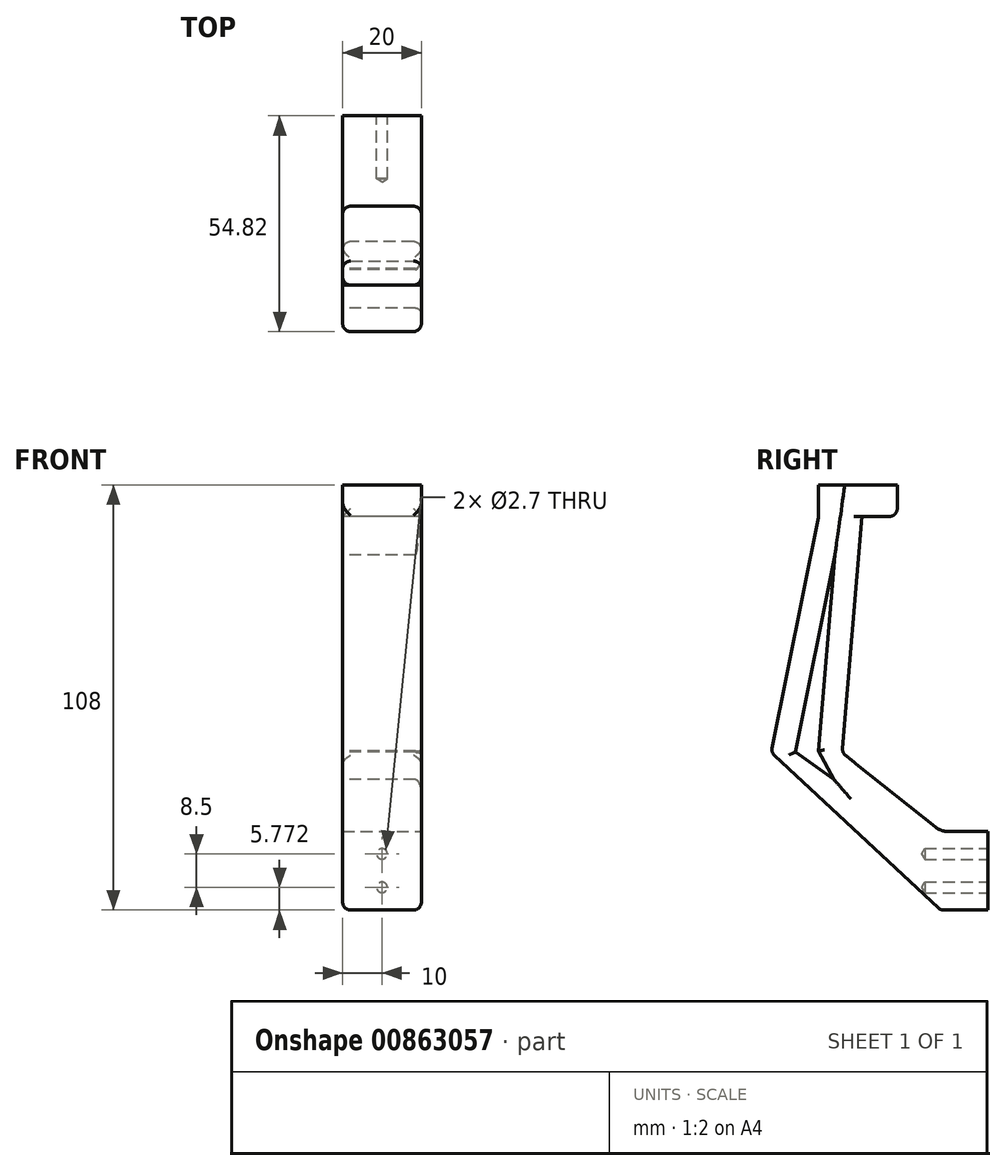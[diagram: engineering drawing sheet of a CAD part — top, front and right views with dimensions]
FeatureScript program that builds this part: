
annotation { "Feature Type Name" : "Feature", "Feature Type Description" : "" }
export const myFeature = defineFeature(function(context is Context, id is Id, definition is map)
    precondition{}
    {
        {
            var Q0;
            Q0=qCreatedBy(makeId("Front.planeOp"),FACE);
            var sketch = newSketch(context, id + "F0", { "sketchPlane" : qUnion([Q0])});
            skLineSegment(sketch, "E0.bottom", {"start": v(-10, -10) * mm, "end": v(10, -10) * mm});
            skLineSegment(sketch, "E0.top", {"start": v(-10, 10) * mm, "end": v(10, 10) * mm});
            skLineSegment(sketch, "E0.left", {"start": v(-10, -10) * mm, "end": v(-10, 10) * mm});
            skLineSegment(sketch, "E0.right", {"start": v(10, -10) * mm, "end": v(10, 10) * mm});
            skPoint(sketch, "E0.middle", {"position": v(0, 0) * mm});
            skSolve(sketch);
        }
        {
            var Q0;
            Q0=qCreatedBy(makeId("Top.planeOp"),FACE);
            cPlane(context, id + "F1", {"entities" : qUnion([Q0]), "cplaneType" : CPlaneType.OFFSET, "offset" : 30 * mm, "width" : 150 * mm, "height" : 150 * mm});
        }
        {
            var Q0;
            Q0=qCreatedBy(id+"F1.planeOp",FACE);
            var sketch = newSketch(context, id + "F2", { "sketchPlane" : qUnion([Q0])});
            skLineSegment(sketch, "E1.bottom", {"start": v(10, -43) * mm, "end": v(-10, -43) * mm});
            skLineSegment(sketch, "E1.top", {"start": v(10, -25) * mm, "end": v(-10, -25) * mm});
            skLineSegment(sketch, "E1.left", {"start": v(10, -43) * mm, "end": v(10, -25) * mm});
            skLineSegment(sketch, "E1.right", {"start": v(-10, -43) * mm, "end": v(-10, -25) * mm});
            skPoint(sketch, "E1.middle", {"position": v(0, -34) * mm});
            skSolve(sketch);
        }
        {
            var Q0;
            Q0=makeQuery(id+"F0.imprint","IMPRINT",FACE,{"disambiguationData":[TD([[makeQuery(id+"F0.imprint","IMPRINT",EDGE,{"derivedFrom":sQuery(id+"F0.wireOp",EDGE,"E0.bottom")}),1.0]])]});
            var Q1;
            Q1=makeQuery(id+"F2.imprint","IMPRINT",FACE,{"disambiguationData":[TD([[makeQuery(id+"F2.imprint","IMPRINT",EDGE,{"derivedFrom":sQuery(id+"F2.wireOp",EDGE,"E1.bottom")}),-1.0]])]});
            loft(context, id + "F3", {"sheetProfilesArray" : [{ "sheetProfileEntities" : qUnion([Q0]) }, { "sheetProfileEntities" : qUnion([Q1]) }]});
        }
        {
            var Q0;
            Q0=qCreatedBy(makeId("Top.planeOp"),FACE);
            cPlane(context, id + "F4", {"entities" : qUnion([Q0]), "cplaneType" : CPlaneType.OFFSET, "offset" : 90 * mm, "width" : 150 * mm, "height" : 150 * mm});
        }
        {
            var Q0;
            Q0=qCreatedBy(id+"F4.planeOp",FACE);
            var sketch = newSketch(context, id + "F5", { "sketchPlane" : qUnion([Q0])});
            skLineSegment(sketch, "E2.bottom", {"start": v(10, -31) * mm, "end": v(-10, -31) * mm});
            skLineSegment(sketch, "E2.top", {"start": v(10, -20) * mm, "end": v(-10, -20) * mm});
            skLineSegment(sketch, "E2.left", {"start": v(10, -31) * mm, "end": v(10, -20) * mm});
            skLineSegment(sketch, "E2.right", {"start": v(-10, -31) * mm, "end": v(-10, -20) * mm});
            skPoint(sketch, "E2.middle", {"position": v(0, -25.5) * mm});
            skSolve(sketch);
        }
        {
            var Q1;
            Q1=makeQuery(id+"F5.imprint","IMPRINT",FACE,{"disambiguationData":[TD([[makeQuery(id+"F5.imprint","IMPRINT",EDGE,{"derivedFrom":sQuery(id+"F5.wireOp",EDGE,"E2.bottom")}),-1.0]])]});
            var Q2;
            Q2=makeQuery(id+"F3.opLoft","CAP_FACE",FACE,{"disambiguationData":[OSD([makeQuery(id+"F2.imprint","IMPRINT",FACE,{"disambiguationData":[TD([[makeQuery(id+"F2.imprint","IMPRINT",EDGE,{"derivedFrom":sQuery(id+"F2.wireOp",EDGE,"E1.bottom")}),-1.0]])]})])],"isStart":true});
            loft(context, id + "F6", {"operationType" : NewBodyOperationType.ADD, "sheetProfilesArray" : [{ "sheetProfileEntities" : qUnion([Q1]) }, { "sheetProfileEntities" : qUnion([Q2]) }]});
        }
        {
            var Q0;
            Q0=qCreatedBy(id+"F4.planeOp",FACE);
            var sketch = newSketch(context, id + "F7", { "sketchPlane" : qUnion([Q0])});
            skLineSegment(sketch, "E3.bottom", {"start": v(10, -31) * mm, "end": v(-10, -31) * mm});
            skLineSegment(sketch, "E3.top", {"start": v(10, -11) * mm, "end": v(-10, -11) * mm});
            skLineSegment(sketch, "E3.left", {"start": v(10, -31) * mm, "end": v(10, -11) * mm});
            skLineSegment(sketch, "E3.right", {"start": v(-10, -31) * mm, "end": v(-10, -11) * mm});
            skPoint(sketch, "E3.middle", {"position": v(0, -21) * mm});
            skSolve(sketch);
        }
        {
            var Q0;
            Q0=makeQuery(id+"F7.imprint","IMPRINT",FACE,{"disambiguationData":[TD([[makeQuery(id+"F7.imprint","IMPRINT",EDGE,{"derivedFrom":sQuery(id+"F7.wireOp",EDGE,"E3.bottom")}),-1.0]])]});
            extrude(context, id + "F8", {"entities" : qUnion([Q0]), "operationType" : NewBodyOperationType.ADD, "depth" : 8 * mm, "offsetDistance" : 25 * mm});
        }
        {
            var Q0;
            Q0=makeQuery(id+"F3.opLoft","CAP_FACE",FACE,{"disambiguationData":[OSD([makeQuery(id+"F0.imprint","IMPRINT",FACE,{"disambiguationData":[TD([[makeQuery(id+"F0.imprint","IMPRINT",EDGE,{"derivedFrom":sQuery(id+"F0.wireOp",EDGE,"E0.bottom")}),1.0]])]})])],"isStart":true});
            extrude(context, id + "F9", {"entities" : qUnion([Q0]), "operationType" : NewBodyOperationType.ADD, "depth" : 12 * mm, "offsetDistance" : 25 * mm});
        }
        {
            var Q0;
            {var subQ0=sQuery(id+"F0.wireOp",EDGE,"E0.right");var subQ1=sQuery(id+"F0.wireOp",EDGE,"E0.left");var subQ2=sQuery(id+"F0.wireOp",EDGE,"E0.top");Q0=makeQuery(id+"F9.boolean.opBoolean","MERGE",EDGE,{"derivedFrom":[makeQuery(id+"F3.opLoft","MID_CAP_EDGE",EDGE,{"disambiguationData":[OSD([subQ2,subQ1,subQ0])],"capPos":0.0}),makeQuery(id+"F9.opExtrude","CAP_EDGE",EDGE,{"disambiguationData":[OSD([subQ2,subQ1,subQ0])],"isStart":true})]});}
            fillet(context, id + "F10", {"entities" : qUnion([Q0]), "radius" : 5 * mm, "tangentPropagation" : true, "allowEdgeOverflow" : false});
        }
        {
            var Q0;
            {var subQ0=sQuery(id+"F0.wireOp",EDGE,"E0.left");var subQ1=sQuery(id+"F0.wireOp",EDGE,"E0.top");var subQ2=sQuery(id+"F0.wireOp",EDGE,"E0.bottom");var subQ3=sQuery(id+"F2.wireOp",EDGE,"E1.right");var subQ4=sQuery(id+"F2.wireOp",EDGE,"E1.top");var subQ5=sQuery(id+"F2.wireOp",EDGE,"E1.bottom");Q0=makeQuery(id+"F9.boolean.opBoolean","MERGE",FACE,{"derivedFrom":[makeQuery(id+"F8.boolean.opBoolean","MERGE",FACE,{"derivedFrom":[makeQuery(id+"F6.boolean.opBoolean","MERGE",FACE,{"derivedFrom":[makeQuery(id+"F3.opLoft","SWEPT_FACE",FACE,{"disambiguationData":[OSD([subQ2,subQ1,subQ0,subQ5,subQ4,subQ3])]}),makeQuery(id+"F6.opLoft","SWEPT_FACE",FACE,{"disambiguationData":[OSD([subQ5,subQ4,subQ3,sQuery(id+"F5.wireOp",EDGE,"E2.bottom"),sQuery(id+"F5.wireOp",EDGE,"E2.top"),sQuery(id+"F5.wireOp",EDGE,"E2.right")])]})]}),makeQuery(id+"F8.opExtrude","SWEPT_FACE",FACE,{"disambiguationData":[OSD([sQuery(id+"F7.wireOp",EDGE,"E3.right")])]})]}),makeQuery(id+"F9.opExtrude","SWEPT_FACE",FACE,{"disambiguationData":[OSD([subQ2,subQ1,subQ0])]})]});}
            var sketch = newSketch(context, id + "F11", { "sketchPlane" : qUnion([Q0])});
            skLineSegment(sketch, "E4.0", {"start": v(26.83, 80.23) * mm, "end": v(30.99, 30.4) * mm});
            skLineSegment(sketch, "E5.0", {"start": v(26.83, 80.23) * mm, "end": v(36.86, 30.12) * mm});
            skLineSegment(sketch, "E6", {"start": v(30.99, 30.4) * mm, "end": v(27.14, 23.2) * mm});
            skLineSegment(sketch, "E7", {"start": v(27.14, 23.2) * mm, "end": v(36.86, 30.12) * mm});
            skSolve(sketch);
        }
        {
            var Q0;
            Q0=makeQuery(id+"F11.imprint","IMPRINT",FACE,{"disambiguationData":[TD([[makeQuery(id+"F11.imprint","IMPRINT",EDGE,{"derivedFrom":sQuery(id+"F11.wireOp",EDGE,"E4.0")}),1.0]])]});
            extrude(context, id + "F12", {"entities" : qUnion([Q0]), "operationType" : NewBodyOperationType.REMOVE, "oppositeDirection" : true, "depth" : 25 * mm, "offsetDistance" : 25 * mm});
        }
        {
            var Q0;
            Q0=makeQuery(id+"F6.opLoft","MID_CAP_EDGE",EDGE,{"disambiguationData":[OSD([sQuery(id+"F5.wireOp",EDGE,"E2.top"),sQuery(id+"F5.wireOp",EDGE,"E2.left"),sQuery(id+"F5.wireOp",EDGE,"E2.right")])],"capPos":0.0});
            var Q1;
            {var subQ0=sQuery(id+"F2.wireOp",EDGE,"E1.right");var subQ1=sQuery(id+"F2.wireOp",EDGE,"E1.left");var subQ2=sQuery(id+"F2.wireOp",EDGE,"E1.top");Q1=makeQuery(id+"F6.boolean.opBoolean","MERGE",EDGE,{"derivedFrom":[makeQuery(id+"F3.opLoft","MID_CAP_EDGE",EDGE,{"disambiguationData":[OSD([subQ2,subQ1,subQ0])],"capPos":1.0}),makeQuery(id+"F6.opLoft","MID_CAP_EDGE",EDGE,{"disambiguationData":[OSD([subQ2,subQ1,subQ0])],"capPos":1.0})]});}
            var Q2;
            {var subQ0=sQuery(id+"F2.wireOp",EDGE,"E1.right");var subQ1=sQuery(id+"F2.wireOp",EDGE,"E1.left");var subQ2=sQuery(id+"F2.wireOp",EDGE,"E1.bottom");Q2=makeQuery(id+"F6.boolean.opBoolean","MERGE",EDGE,{"derivedFrom":[makeQuery(id+"F3.opLoft","MID_CAP_EDGE",EDGE,{"disambiguationData":[OSD([subQ2,subQ1,subQ0])],"capPos":1.0}),makeQuery(id+"F6.opLoft","MID_CAP_EDGE",EDGE,{"disambiguationData":[OSD([subQ2,subQ1,subQ0])],"capPos":1.0})]});}
            var Q3;
            Q3=makeQuery(id+"F6.opLoft","SWEPT_EDGE",EDGE,{"disambiguationData":[OSD([sQuery(id+"F2.wireOp",EDGE,"E1.bottom"),sQuery(id+"F2.wireOp",EDGE,"E1.left"),sQuery(id+"F5.wireOp",EDGE,"E2.bottom"),sQuery(id+"F5.wireOp",EDGE,"E2.left")])]});
            var Q4;
            Q4=makeQuery(id+"F3.opLoft","SWEPT_EDGE",EDGE,{"disambiguationData":[OSD([sQuery(id+"F0.wireOp",EDGE,"E0.bottom"),sQuery(id+"F0.wireOp",EDGE,"E0.right"),sQuery(id+"F2.wireOp",EDGE,"E1.bottom"),sQuery(id+"F2.wireOp",EDGE,"E1.left")])]});
            var Q5;
            Q5=makeQuery(id+"F3.opLoft","SWEPT_EDGE",EDGE,{"disambiguationData":[OSD([sQuery(id+"F0.wireOp",EDGE,"E0.bottom"),sQuery(id+"F0.wireOp",EDGE,"E0.left"),sQuery(id+"F2.wireOp",EDGE,"E1.bottom"),sQuery(id+"F2.wireOp",EDGE,"E1.right")])]});
            var Q6;
            Q6=makeQuery(id+"F6.opLoft","SWEPT_EDGE",EDGE,{"disambiguationData":[OSD([sQuery(id+"F2.wireOp",EDGE,"E1.bottom"),sQuery(id+"F2.wireOp",EDGE,"E1.right"),sQuery(id+"F5.wireOp",EDGE,"E2.bottom"),sQuery(id+"F5.wireOp",EDGE,"E2.right")])]});
            var Q7;
            Q7=makeQuery(id+"F8.opExtrude","SWEPT_EDGE",EDGE,{"disambiguationData":[OSD([sQuery(id+"F7.wireOp",EDGE,"E3.top"),sQuery(id+"F7.wireOp",EDGE,"E3.right")])]});
            var Q8;
            Q8=makeQuery(id+"F8.opExtrude","SWEPT_EDGE",EDGE,{"disambiguationData":[OSD([sQuery(id+"F7.wireOp",EDGE,"E3.top"),sQuery(id+"F7.wireOp",EDGE,"E3.left")])]});
            var Q9;
            Q9=makeQuery(id+"F6.opLoft","SWEPT_EDGE",EDGE,{"disambiguationData":[OSD([sQuery(id+"F2.wireOp",EDGE,"E1.top"),sQuery(id+"F2.wireOp",EDGE,"E1.left"),sQuery(id+"F5.wireOp",EDGE,"E2.top"),sQuery(id+"F5.wireOp",EDGE,"E2.left")])]});
            var Q10;
            Q10=makeQuery(id+"F6.opLoft","SWEPT_EDGE",EDGE,{"disambiguationData":[OSD([sQuery(id+"F2.wireOp",EDGE,"E1.top"),sQuery(id+"F2.wireOp",EDGE,"E1.right"),sQuery(id+"F5.wireOp",EDGE,"E2.top"),sQuery(id+"F5.wireOp",EDGE,"E2.right")])]});
            var Q11;
            Q11=makeQuery(id+"F9.opExtrude","SWEPT_EDGE",EDGE,{"disambiguationData":[OSD([sQuery(id+"F0.wireOp",EDGE,"E0.bottom"),sQuery(id+"F0.wireOp",EDGE,"E0.right")])]});
            var Q12;
            Q12=makeQuery(id+"F9.opExtrude","SWEPT_EDGE",EDGE,{"disambiguationData":[OSD([sQuery(id+"F0.wireOp",EDGE,"E0.bottom"),sQuery(id+"F0.wireOp",EDGE,"E0.left")])]});
            var Q13;
            Q13=makeQuery(id+"F8.opExtrude","CAP_EDGE",EDGE,{"disambiguationData":[OSD([sQuery(id+"F7.wireOp",EDGE,"E3.top")])],"isStart":true});
            var Q14;
            Q14=makeQuery(id+"F8.boolean.opBoolean","MERGE",EDGE,{"derivedFrom":[makeQuery(id+"F6.opLoft","MID_CAP_EDGE",EDGE,{"disambiguationData":[OSD([sQuery(id+"F5.wireOp",EDGE,"E2.bottom"),sQuery(id+"F5.wireOp",EDGE,"E2.left"),sQuery(id+"F5.wireOp",EDGE,"E2.right")])],"capPos":0.0}),makeQuery(id+"F8.opExtrude","CAP_EDGE",EDGE,{"disambiguationData":[OSD([sQuery(id+"F7.wireOp",EDGE,"E3.bottom")])],"isStart":true})]});
            var Q15;
            {var subQ0=sQuery(id+"F0.wireOp",EDGE,"E0.right");var subQ1=sQuery(id+"F0.wireOp",EDGE,"E0.left");var subQ2=sQuery(id+"F0.wireOp",EDGE,"E0.bottom");Q15=makeQuery(id+"F9.boolean.opBoolean","MERGE",EDGE,{"derivedFrom":[makeQuery(id+"F3.opLoft","MID_CAP_EDGE",EDGE,{"disambiguationData":[OSD([subQ2,subQ1,subQ0])],"capPos":0.0}),makeQuery(id+"F9.opExtrude","CAP_EDGE",EDGE,{"disambiguationData":[OSD([subQ2,subQ1,subQ0])],"isStart":true})]});}
            fillet(context, id + "F13", {"entities" : qUnion([Q0, Q1, Q2, Q3, Q4, Q5, Q6, Q7, Q8, Q9, Q10, Q11, Q12, Q13, Q14, Q15]), "radius" : 2 * mm, "tangentPropagation" : true, "allowEdgeOverflow" : false});
        }
        {
            var Q0;
            Q0=makeQuery(id+"F12.boolean.opBoolean","COPY",EDGE,{"derivedFrom":makeQuery(id+"F12.opExtrude","CAP_EDGE",EDGE,{"disambiguationData":[OSD([sQuery(id+"F11.wireOp",EDGE,"E4.0")])],"isStart":true})});
            var Q1;
            Q1=makeQuery(id+"F12.boolean.opBoolean","COPY",EDGE,{"derivedFrom":makeQuery(id+"F12.opExtrude","CAP_EDGE",EDGE,{"disambiguationData":[OSD([sQuery(id+"F11.wireOp",EDGE,"E5.0")])],"isStart":true})});
            var Q2;
            Q2=makeQuery(id+"F12.boolean.opBoolean","COPY",EDGE,{"derivedFrom":makeQuery(id+"F12.opExtrude","CAP_EDGE",EDGE,{"disambiguationData":[OSD([sQuery(id+"F11.wireOp",EDGE,"E7")])],"isStart":true})});
            var Q3;
            Q3=makeQuery(id+"F12.boolean.opBoolean","COPY",EDGE,{"derivedFrom":makeQuery(id+"F12.opExtrude","CAP_EDGE",EDGE,{"disambiguationData":[OSD([sQuery(id+"F11.wireOp",EDGE,"E6")])],"isStart":true})});
            var Q4;
            {var subQ0=sQuery(id+"F0.wireOp",EDGE,"E0.right");var subQ1=sQuery(id+"F0.wireOp",EDGE,"E0.top");var subQ2=sQuery(id+"F0.wireOp",EDGE,"E0.bottom");var subQ3=sQuery(id+"F2.wireOp",EDGE,"E1.left");var subQ4=sQuery(id+"F2.wireOp",EDGE,"E1.top");var subQ5=sQuery(id+"F2.wireOp",EDGE,"E1.bottom");Q4=makeQuery(id+"F12.boolean.opBoolean","INTERSECT",EDGE,{"derivedFrom":[makeQuery(id+"F9.boolean.opBoolean","MERGE",FACE,{"derivedFrom":[makeQuery(id+"F8.boolean.opBoolean","MERGE",FACE,{"derivedFrom":[makeQuery(id+"F6.boolean.opBoolean","MERGE",FACE,{"derivedFrom":[makeQuery(id+"F3.opLoft","SWEPT_FACE",FACE,{"disambiguationData":[OSD([subQ2,subQ1,subQ0,subQ5,subQ4,subQ3])]}),makeQuery(id+"F6.opLoft","SWEPT_FACE",FACE,{"disambiguationData":[OSD([subQ5,subQ4,subQ3,sQuery(id+"F5.wireOp",EDGE,"E2.bottom"),sQuery(id+"F5.wireOp",EDGE,"E2.top"),sQuery(id+"F5.wireOp",EDGE,"E2.left")])]})]}),makeQuery(id+"F8.opExtrude","SWEPT_FACE",FACE,{"disambiguationData":[OSD([sQuery(id+"F7.wireOp",EDGE,"E3.left")])]})]}),makeQuery(id+"F9.opExtrude","SWEPT_FACE",FACE,{"disambiguationData":[OSD([subQ2,subQ1,subQ0])]})]}),makeQuery(id+"F12.opExtrude","SWEPT_FACE",FACE,{"disambiguationData":[OSD([sQuery(id+"F11.wireOp",EDGE,"E7")])]})]});}
            var Q5;
            {var subQ0=sQuery(id+"F0.wireOp",EDGE,"E0.right");var subQ1=sQuery(id+"F0.wireOp",EDGE,"E0.top");var subQ2=sQuery(id+"F0.wireOp",EDGE,"E0.bottom");var subQ3=sQuery(id+"F2.wireOp",EDGE,"E1.left");var subQ4=sQuery(id+"F2.wireOp",EDGE,"E1.top");var subQ5=sQuery(id+"F2.wireOp",EDGE,"E1.bottom");Q5=makeQuery(id+"F12.boolean.opBoolean","INTERSECT",EDGE,{"derivedFrom":[makeQuery(id+"F9.boolean.opBoolean","MERGE",FACE,{"derivedFrom":[makeQuery(id+"F8.boolean.opBoolean","MERGE",FACE,{"derivedFrom":[makeQuery(id+"F6.boolean.opBoolean","MERGE",FACE,{"derivedFrom":[makeQuery(id+"F3.opLoft","SWEPT_FACE",FACE,{"disambiguationData":[OSD([subQ2,subQ1,subQ0,subQ5,subQ4,subQ3])]}),makeQuery(id+"F6.opLoft","SWEPT_FACE",FACE,{"disambiguationData":[OSD([subQ5,subQ4,subQ3,sQuery(id+"F5.wireOp",EDGE,"E2.bottom"),sQuery(id+"F5.wireOp",EDGE,"E2.top"),sQuery(id+"F5.wireOp",EDGE,"E2.left")])]})]}),makeQuery(id+"F8.opExtrude","SWEPT_FACE",FACE,{"disambiguationData":[OSD([sQuery(id+"F7.wireOp",EDGE,"E3.left")])]})]}),makeQuery(id+"F9.opExtrude","SWEPT_FACE",FACE,{"disambiguationData":[OSD([subQ2,subQ1,subQ0])]})]}),makeQuery(id+"F12.opExtrude","SWEPT_FACE",FACE,{"disambiguationData":[OSD([sQuery(id+"F11.wireOp",EDGE,"E6")])]})]});}
            var Q6;
            {var subQ0=sQuery(id+"F0.wireOp",EDGE,"E0.right");var subQ1=sQuery(id+"F0.wireOp",EDGE,"E0.top");var subQ2=sQuery(id+"F0.wireOp",EDGE,"E0.bottom");var subQ3=sQuery(id+"F2.wireOp",EDGE,"E1.left");var subQ4=sQuery(id+"F2.wireOp",EDGE,"E1.top");var subQ5=sQuery(id+"F2.wireOp",EDGE,"E1.bottom");Q6=makeQuery(id+"F12.boolean.opBoolean","INTERSECT",EDGE,{"derivedFrom":[makeQuery(id+"F9.boolean.opBoolean","MERGE",FACE,{"derivedFrom":[makeQuery(id+"F8.boolean.opBoolean","MERGE",FACE,{"derivedFrom":[makeQuery(id+"F6.boolean.opBoolean","MERGE",FACE,{"derivedFrom":[makeQuery(id+"F3.opLoft","SWEPT_FACE",FACE,{"disambiguationData":[OSD([subQ2,subQ1,subQ0,subQ5,subQ4,subQ3])]}),makeQuery(id+"F6.opLoft","SWEPT_FACE",FACE,{"disambiguationData":[OSD([subQ5,subQ4,subQ3,sQuery(id+"F5.wireOp",EDGE,"E2.bottom"),sQuery(id+"F5.wireOp",EDGE,"E2.top"),sQuery(id+"F5.wireOp",EDGE,"E2.left")])]})]}),makeQuery(id+"F8.opExtrude","SWEPT_FACE",FACE,{"disambiguationData":[OSD([sQuery(id+"F7.wireOp",EDGE,"E3.left")])]})]}),makeQuery(id+"F9.opExtrude","SWEPT_FACE",FACE,{"disambiguationData":[OSD([subQ2,subQ1,subQ0])]})]}),makeQuery(id+"F12.opExtrude","SWEPT_FACE",FACE,{"disambiguationData":[OSD([sQuery(id+"F11.wireOp",EDGE,"E4.0")])]})]});}
            var Q7;
            {var subQ0=sQuery(id+"F0.wireOp",EDGE,"E0.right");var subQ1=sQuery(id+"F0.wireOp",EDGE,"E0.top");var subQ2=sQuery(id+"F0.wireOp",EDGE,"E0.bottom");var subQ3=sQuery(id+"F2.wireOp",EDGE,"E1.left");var subQ4=sQuery(id+"F2.wireOp",EDGE,"E1.top");var subQ5=sQuery(id+"F2.wireOp",EDGE,"E1.bottom");Q7=makeQuery(id+"F12.boolean.opBoolean","INTERSECT",EDGE,{"derivedFrom":[makeQuery(id+"F9.boolean.opBoolean","MERGE",FACE,{"derivedFrom":[makeQuery(id+"F8.boolean.opBoolean","MERGE",FACE,{"derivedFrom":[makeQuery(id+"F6.boolean.opBoolean","MERGE",FACE,{"derivedFrom":[makeQuery(id+"F3.opLoft","SWEPT_FACE",FACE,{"disambiguationData":[OSD([subQ2,subQ1,subQ0,subQ5,subQ4,subQ3])]}),makeQuery(id+"F6.opLoft","SWEPT_FACE",FACE,{"disambiguationData":[OSD([subQ5,subQ4,subQ3,sQuery(id+"F5.wireOp",EDGE,"E2.bottom"),sQuery(id+"F5.wireOp",EDGE,"E2.top"),sQuery(id+"F5.wireOp",EDGE,"E2.left")])]})]}),makeQuery(id+"F8.opExtrude","SWEPT_FACE",FACE,{"disambiguationData":[OSD([sQuery(id+"F7.wireOp",EDGE,"E3.left")])]})]}),makeQuery(id+"F9.opExtrude","SWEPT_FACE",FACE,{"disambiguationData":[OSD([subQ2,subQ1,subQ0])]})]}),makeQuery(id+"F12.opExtrude","SWEPT_FACE",FACE,{"disambiguationData":[OSD([sQuery(id+"F11.wireOp",EDGE,"E5.0")])]})]});}
            fillet(context, id + "F14", {"entities" : qUnion([Q0, Q1, Q2, Q3, Q4, Q5, Q6, Q7]), "radius" : 1.5 * mm, "tangentPropagation" : true, "allowEdgeOverflow" : false});
        }
        {
            var Q0;
            Q0=makeQuery(id+"F9.opExtrude","CAP_FACE",FACE,{"disambiguationData":[OSD([makeQuery(id+"F0.imprint","IMPRINT",FACE,{"disambiguationData":[TD([[makeQuery(id+"F0.imprint","IMPRINT",EDGE,{"derivedFrom":sQuery(id+"F0.wireOp",EDGE,"E0.bottom")}),1.0]])]})])],"isStart":false});
            var sketch = newSketch(context, id + "F15", { "sketchPlane" : qUnion([Q0])});
            skPoint(sketch, "E8", {"position": v(0, 4.27) * mm});
            skPoint(sketch, "E9", {"position": v(0, -4.23) * mm});
            skSolve(sketch);
        }
        {
            var Q0;
            Q0=sQuery(id+"F15.wireOp",VERTEX,"E8");
            var Q1;
            Q1=sQuery(id+"F15.wireOp",VERTEX,"E9");
            var Q2;
            Q2=makeQuery(id+"F3.opLoft","SWEPT_BODY",BODY,{"disambiguationData":[OSD([makeQuery(id+"F0.imprint","IMPRINT",FACE,{"disambiguationData":[TD([[makeQuery(id+"F0.imprint","IMPRINT",EDGE,{"derivedFrom":sQuery(id+"F0.wireOp",EDGE,"E0.bottom")}),1.0]])]}),makeQuery(id+"F2.imprint","IMPRINT",FACE,{"disambiguationData":[TD([[makeQuery(id+"F2.imprint","IMPRINT",EDGE,{"derivedFrom":sQuery(id+"F2.wireOp",EDGE,"E1.bottom")}),-1.0]])]})])]});
            hole(context, id + "F16", {"style" : HoleStyle.SIMPLE, "endStyle" : HoleEndStyle.BLIND, "holeDiameter" : 2.7 * mm, "majorDiameter" : 5 * mm, "holeDepth" : 16 * mm, "isTappedThrough" : true, "tappedDepth" : 12 * mm, "tapClearance" : 3, "locations" : qUnion([Q0, Q1]), "scope" : qUnion([Q2])});
        }
    });
